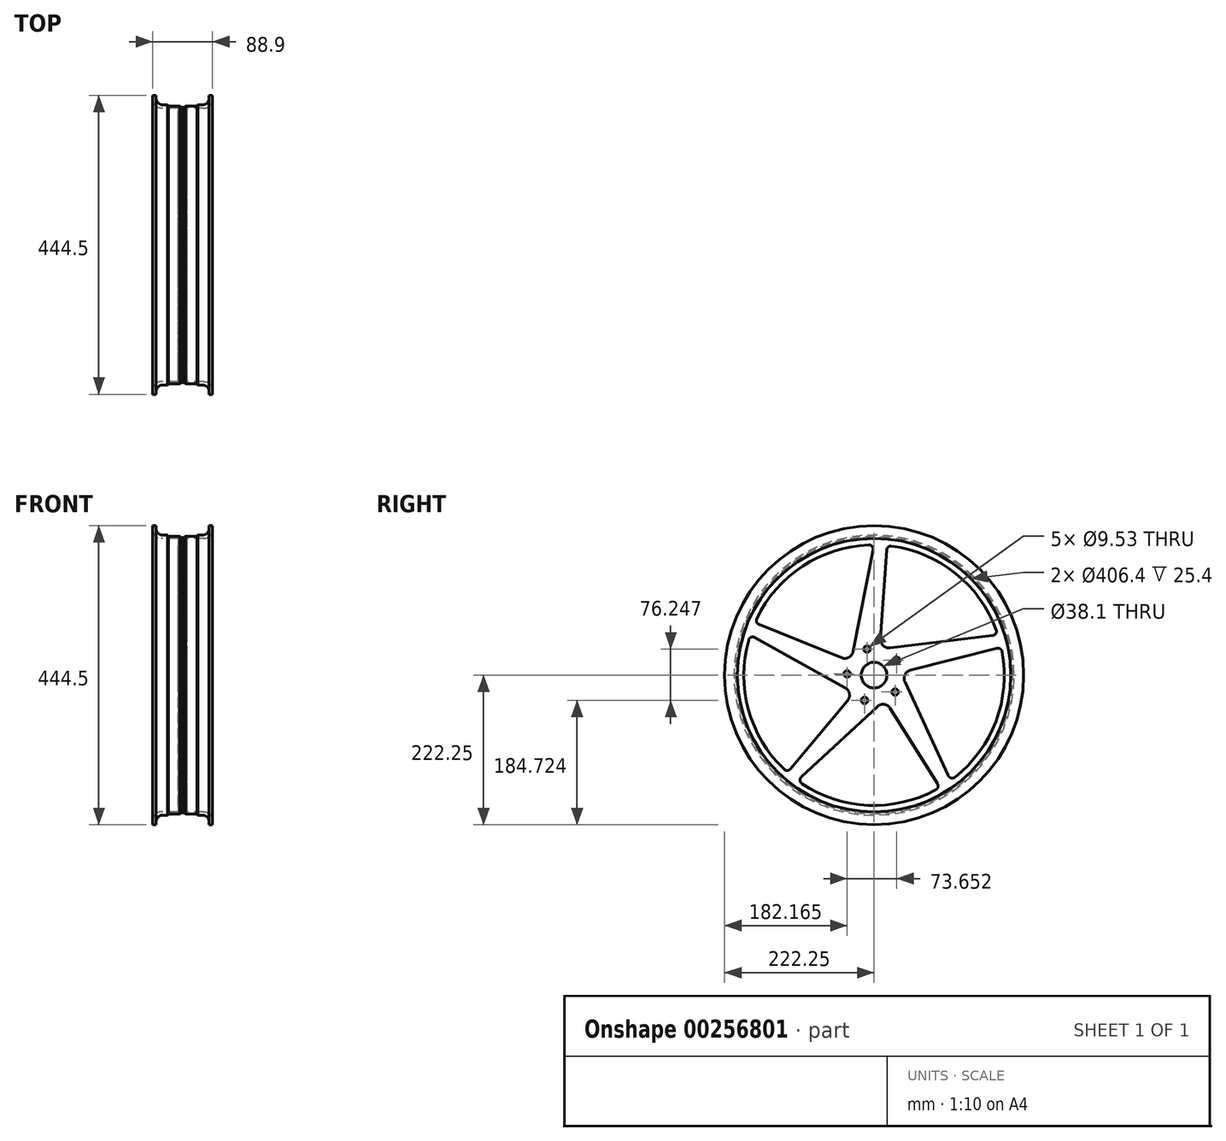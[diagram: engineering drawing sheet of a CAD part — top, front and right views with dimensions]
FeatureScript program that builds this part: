
annotation { "Feature Type Name" : "Feature", "Feature Type Description" : "" }
export const myFeature = defineFeature(function(context is Context, id is Id, definition is map)
    precondition{}
    {
        {
            var Q0;
            Q0=qCreatedBy(makeId("Top.planeOp"),FACE);
            var sketch = newSketch(context, id + "F0", { "sketchPlane" : qUnion([Q0])});
            skLineSegment(sketch, "E0.0", {"start": v(-6.35, 0) * mm, "end": v(-6.35, -203.2) * mm});
            skLineSegment(sketch, "E1.0", {"start": v(6.35, 0) * mm, "end": v(6.35, -203.2) * mm});
            skLineSegment(sketch, "E2", {"start": v(6.35, -203.2) * mm, "end": v(31.75, -203.2) * mm});
            skLineSegment(sketch, "E3", {"start": v(44.45, -215.9) * mm, "end": v(44.45, -222.25) * mm});
            skLineSegment(sketch, "E4", {"start": v(-6.35, -203.2) * mm, "end": v(-31.75, -203.2) * mm});
            skLineSegment(sketch, "E5", {"start": v(44.45, -222.25) * mm, "end": v(39.37, -222.25) * mm});
            skLineSegment(sketch, "E6", {"start": v(-44.45, -215.9) * mm, "end": v(-44.45, -222.25) * mm});
            skLineSegment(sketch, "E7.0", {"start": v(-22.55, -208.28) * mm, "end": v(-29.84, -208.28) * mm});
            skLineSegment(sketch, "E8.0", {"start": v(-39.37, -217.8) * mm, "end": v(-39.37, -222.25) * mm});
            skLineSegment(sketch, "E9.0", {"start": v(39.37, -217.8) * mm, "end": v(39.37, -222.25) * mm});
            skLineSegment(sketch, "E10.trimOffspring", {"start": v(-39.37, -222.25) * mm, "end": v(-44.45, -222.25) * mm});
            skPoint(sketch, "E11.visualSharp", {"position": v(-44.45, -203.2) * mm});
            skArc(sketch, "E11.filletArc", {"start": v(-31.75, -203.2) * mm, "mid": v(-40.73, -206.92) * mm, "end": v(-44.45, -215.9) * mm});
            skPoint(sketch, "E12.visualSharp", {"position": v(-39.37, -208.28) * mm});
            skArc(sketch, "E12.filletArc", {"start": v(-29.84, -208.28) * mm, "mid": v(-36.58, -211.07) * mm, "end": v(-39.37, -217.8) * mm});
            skPoint(sketch, "E13.visualSharp", {"position": v(39.37, -208.28) * mm});
            skArc(sketch, "E13.filletArc", {"start": v(39.37, -217.8) * mm, "mid": v(36.58, -211.07) * mm, "end": v(29.85, -208.28) * mm});
            skPoint(sketch, "E14.visualSharp", {"position": v(44.45, -203.2) * mm});
            skArc(sketch, "E14.filletArc", {"start": v(44.45, -215.9) * mm, "mid": v(40.73, -206.92) * mm, "end": v(31.75, -203.2) * mm});
            skLineSegment(sketch, "E15", {"start": v(29.85, -208.28) * mm, "end": v(22.55, -208.28) * mm});
            skLineSegment(sketch, "E16", {"start": v(-6.35, 0) * mm, "end": v(6.35, 0) * mm});
            skLineSegment(sketch, "E17", {"start": v(-22.55, -208.28) * mm, "end": v(-21.34, -206.26) * mm});
            skLineSegment(sketch, "E18", {"start": v(-21.34, -206.26) * mm, "end": v(-4.07, -206.26) * mm});
            skLineSegment(sketch, "E19", {"start": v(-4.07, -206.26) * mm, "end": v(-2.24, -204.5) * mm});
            skLineSegment(sketch, "E20", {"start": v(-2.24, -204.5) * mm, "end": v(0, -204.5) * mm});
            skLineSegment(sketch, "E21.MirrorCS", {"start": v(22.55, -208.28) * mm, "end": v(21.34, -206.26) * mm});
            skLineSegment(sketch, "E22.MirrorCS", {"start": v(21.34, -206.26) * mm, "end": v(4.07, -206.26) * mm});
            skLineSegment(sketch, "E23.MirrorCS", {"start": v(2.24, -204.5) * mm, "end": v(0, -204.5) * mm});
            skLineSegment(sketch, "E24.MirrorCS", {"start": v(4.07, -206.26) * mm, "end": v(2.24, -204.5) * mm});
            skPoint(sketch, "E25.end.orphan", {"position": v(0, -208.28) * mm});
            skSolve(sketch);
        }
        {
            var Q0;
            Q0=makeQuery(id+"F0.imprint","IMPRINT",FACE,{"disambiguationData":[TD([[makeQuery(id+"F0.imprint","IMPRINT",EDGE,{"derivedFrom":sQuery(id+"F0.wireOp",EDGE,"E0.0")}),1.0]])]});
            var Q1;
            Q1=sQuery(id+"F0.wireOp",EDGE,"E16");
            revolve(context, id + "F1", {"entities" : qUnion([Q0]), "axis" : qUnion([Q1]), "revolveType" : RevolveType.FULL});
        }
        {
            var Q0;
            Q0=makeQuery(id+"F1.opRevolve","SWEPT_FACE",FACE,{"disambiguationData":[OSD([sQuery(id+"F0.wireOp",EDGE,"E0.0")])]});
            var sketch = newSketch(context, id + "F2", { "sketchPlane" : qUnion([Q0])});
            skCircle(sketch, "E26", {"center": v(0, 0) * mm, "radius": 19.05 * mm});
            skArc(sketch, "E27", {"start": v(-25.92, 191.93) * mm, "mid": v(-120.99, 151.23) * mm, "end": v(-181.56, 67.42) * mm});
            skLineSegment(sketch, "E28", {"start": v(-9.61, 54) * mm, "end": v(-18.74, 186.08) * mm});
            skLineSegment(sketch, "E29.1.0", {"start": v(-54.33, 7.55) * mm, "end": v(-182.76, 39.68) * mm});
            skLineSegment(sketch, "E29.2.0", {"start": v(-23.97, -49.34) * mm, "end": v(-94.21, -161.55) * mm});
            skLineSegment(sketch, "E29.3.0", {"start": v(39.52, -38.04) * mm, "end": v(124.53, -139.52) * mm});
            skLineSegment(sketch, "E29.4.0", {"start": v(48.4, 25.83) * mm, "end": v(171.18, 75.32) * mm});
            skLineSegment(sketch, "E30.trimOffspring", {"start": v(-23.8, 40.52) * mm, "end": v(-176.37, 58.9) * mm});
            skPoint(sketch, "E31.orphan", {"position": v(-8.45, 37.15) * mm});
            skLineSegment(sketch, "E32.trimOffspring", {"start": v(-45.9, -10.11) * mm, "end": v(-110.52, -149.53) * mm});
            skPoint(sketch, "E33.orphan", {"position": v(-37.94, 3.45) * mm});
            skLineSegment(sketch, "E34.trimOffspring", {"start": v(31.18, 35.16) * mm, "end": v(1.52, 185.94) * mm});
            skPoint(sketch, "E35.orphan", {"position": v(32.72, 19.51) * mm});
            skLineSegment(sketch, "E36.trimOffspring", {"start": v(43.07, -18.8) * mm, "end": v(177.3, 56.01) * mm});
            skPoint(sketch, "E37.orphan", {"position": v(28.67, -25.1) * mm});
            skPoint(sketch, "E38.orphan", {"position": v(-15, -35.02) * mm});
            skLineSegment(sketch, "E39.trimOffspring", {"start": v(-4.56, -46.77) * mm, "end": v(108.06, -151.32) * mm});
            skPoint(sketch, "E40.visualSharp", {"position": v(-39.43, 3.82) * mm});
            skArc(sketch, "E40.filletArc", {"start": v(-45.9, -10.11) * mm, "mid": v(-45.96, 0.7) * mm, "end": v(-54.33, 7.55) * mm});
            skPoint(sketch, "E41.visualSharp", {"position": v(-8.55, 38.68) * mm});
            skArc(sketch, "E41.filletArc", {"start": v(-23.8, 40.52) * mm, "mid": v(-13.53, 43.92) * mm, "end": v(-9.61, 54) * mm});
            skPoint(sketch, "E42.visualSharp", {"position": v(34.15, 20.09) * mm});
            skArc(sketch, "E42.filletArc", {"start": v(31.18, 35.16) * mm, "mid": v(37.6, 26.44) * mm, "end": v(48.4, 25.83) * mm});
            skPoint(sketch, "E43.visualSharp", {"position": v(29.66, -26.27) * mm});
            skArc(sketch, "E43.filletArc", {"start": v(43.07, -18.8) * mm, "mid": v(36.77, -27.58) * mm, "end": v(39.52, -38.04) * mm});
            skPoint(sketch, "E44.visualSharp", {"position": v(-15.82, -36.32) * mm});
            skArc(sketch, "E44.filletArc", {"start": v(-4.56, -46.77) * mm, "mid": v(-14.87, -43.49) * mm, "end": v(-23.97, -49.34) * mm});
            skArc(sketch, "E45.trimOffspring", {"start": v(174.53, 83.97) * mm, "mid": v(106.44, 161.8) * mm, "end": v(8.02, 193.5) * mm});
            skArc(sketch, "E46.trimOffspring", {"start": v(-190.55, 34.65) * mm, "mid": v(-181.22, -68.33) * mm, "end": v(-120.23, -151.84) * mm});
            skArc(sketch, "E47.trimOffspring", {"start": v(-91.84, -170.51) * mm, "mid": v(8.99, -193.47) * mm, "end": v(107.26, -161.26) * mm});
            skArc(sketch, "E48.trimOffspring", {"start": v(133.79, -140.04) * mm, "mid": v(186.78, -51.23) * mm, "end": v(186.51, 52.17) * mm});
            skPoint(sketch, "E49.visualSharp", {"position": v(-184.2, 59.85) * mm});
            skArc(sketch, "E49.filletArc", {"start": v(-181.56, 67.42) * mm, "mid": v(-181.03, 61.9) * mm, "end": v(-176.37, 58.9) * mm});
            skPoint(sketch, "E50.visualSharp", {"position": v(-189.22, 41.3) * mm});
            skArc(sketch, "E50.filletArc", {"start": v(-182.76, 39.68) * mm, "mid": v(-187.74, 38.85) * mm, "end": v(-190.55, 34.65) * mm});
            skPoint(sketch, "E51.visualSharp", {"position": v(-19.2, 192.72) * mm});
            skArc(sketch, "E51.filletArc", {"start": v(-18.74, 186.08) * mm, "mid": v(-21.06, 190.56) * mm, "end": v(-25.92, 191.93) * mm});
            skPoint(sketch, "E52.visualSharp", {"position": v(0, 193.68) * mm});
            skArc(sketch, "E52.filletArc", {"start": v(8.02, 193.5) * mm, "mid": v(2.93, 191.3) * mm, "end": v(1.52, 185.94) * mm});
            skPoint(sketch, "E53.visualSharp", {"position": v(177.36, 77.81) * mm});
            skArc(sketch, "E53.filletArc", {"start": v(171.18, 75.32) * mm, "mid": v(174.73, 78.92) * mm, "end": v(174.53, 83.97) * mm});
            skPoint(sketch, "E54.visualSharp", {"position": v(184.2, 59.85) * mm});
            skArc(sketch, "E54.filletArc", {"start": v(186.51, 52.17) * mm, "mid": v(182.84, 56.33) * mm, "end": v(177.3, 56.01) * mm});
            skPoint(sketch, "E55.visualSharp", {"position": v(128.81, -144.63) * mm});
            skArc(sketch, "E55.filletArc", {"start": v(124.53, -139.52) * mm, "mid": v(129.05, -141.79) * mm, "end": v(133.79, -140.04) * mm});
            skPoint(sketch, "E56.visualSharp", {"position": v(113.84, -156.69) * mm});
            skArc(sketch, "E56.filletArc", {"start": v(107.26, -161.26) * mm, "mid": v(110.07, -156.49) * mm, "end": v(108.06, -151.32) * mm});
            skPoint(sketch, "E57.visualSharp", {"position": v(-97.75, -167.2) * mm});
            skArc(sketch, "E57.filletArc", {"start": v(-94.21, -161.55) * mm, "mid": v(-94.97, -166.55) * mm, "end": v(-91.84, -170.51) * mm});
            skPoint(sketch, "E58.visualSharp", {"position": v(-113.84, -156.69) * mm});
            skArc(sketch, "E58.filletArc", {"start": v(-120.23, -151.84) * mm, "mid": v(-114.82, -153.04) * mm, "end": v(-110.52, -149.53) * mm});
            skSolve(sketch);
        }
        {
            var Q0;
            Q0=makeQuery(id+"F2.imprint","IMPRINT",FACE,{"disambiguationData":[TD([[makeQuery(id+"F2.imprint","IMPRINT",EDGE,{"derivedFrom":sQuery(id+"F2.wireOp",EDGE,"E26")}),1.0]])]});
            var Q1;
            Q1=makeQuery(id+"F2.imprint","IMPRINT",FACE,{"disambiguationData":[TD([[makeQuery(id+"F2.imprint","IMPRINT",EDGE,{"derivedFrom":sQuery(id+"F2.wireOp",EDGE,"E27")}),1.0]])]});
            var Q2;
            Q2=makeQuery(id+"F2.imprint","IMPRINT",FACE,{"disambiguationData":[TD([[makeQuery(id+"F2.imprint","IMPRINT",EDGE,{"derivedFrom":sQuery(id+"F2.wireOp",EDGE,"E29.1.0")}),1.0]])]});
            var Q3;
            Q3=makeQuery(id+"F2.imprint","IMPRINT",FACE,{"disambiguationData":[TD([[makeQuery(id+"F2.imprint","IMPRINT",EDGE,{"derivedFrom":sQuery(id+"F2.wireOp",EDGE,"E29.2.0")}),1.0]])]});
            var Q4;
            Q4=makeQuery(id+"F2.imprint","IMPRINT",FACE,{"disambiguationData":[TD([[makeQuery(id+"F2.imprint","IMPRINT",EDGE,{"derivedFrom":sQuery(id+"F2.wireOp",EDGE,"E29.3.0")}),1.0]])]});
            var Q5;
            Q5=makeQuery(id+"F2.imprint","IMPRINT",FACE,{"disambiguationData":[TD([[makeQuery(id+"F2.imprint","IMPRINT",EDGE,{"derivedFrom":sQuery(id+"F2.wireOp",EDGE,"E29.4.0")}),1.0]])]});
            extrude(context, id + "F3", {"entities" : qUnion([Q0, Q1, Q2, Q3, Q4, Q5]), "operationType" : NewBodyOperationType.REMOVE, "endBound" : BoundingType.THROUGH_ALL, "oppositeDirection" : true, "depth" : 25.4 * mm});
        }
        {
            var Q0;
            Q0=makeQuery(id+"F3.boolean.opBoolean","COPY",EDGE,{"derivedFrom":makeQuery(id+"F3.opExtrude","CAP_EDGE",EDGE,{"disambiguationData":[OSD([sQuery(id+"F2.wireOp",EDGE,"E30.trimOffspring")])],"isStart":true})});
            var Q1;
            Q1=makeQuery(id+"F3.boolean.opBoolean","COPY",EDGE,{"derivedFrom":makeQuery(id+"F3.opExtrude","CAP_EDGE",EDGE,{"disambiguationData":[OSD([sQuery(id+"F2.wireOp",EDGE,"E34.trimOffspring")])],"isStart":true})});
            var Q2;
            Q2=makeQuery(id+"F3.boolean.opBoolean","COPY",EDGE,{"derivedFrom":makeQuery(id+"F3.opExtrude","CAP_EDGE",EDGE,{"disambiguationData":[OSD([sQuery(id+"F2.wireOp",EDGE,"E36.trimOffspring")])],"isStart":true})});
            var Q3;
            Q3=makeQuery(id+"F3.boolean.opBoolean","COPY",EDGE,{"derivedFrom":makeQuery(id+"F3.opExtrude","CAP_EDGE",EDGE,{"disambiguationData":[OSD([sQuery(id+"F2.wireOp",EDGE,"E29.2.0")])],"isStart":true})});
            var Q4;
            Q4=makeQuery(id+"F3.boolean.opBoolean","COPY",EDGE,{"derivedFrom":makeQuery(id+"F3.opExtrude","CAP_EDGE",EDGE,{"disambiguationData":[OSD([sQuery(id+"F2.wireOp",EDGE,"E32.trimOffspring")])],"isStart":true})});
            var Q5;
            Q5=makeQuery(id+"F3.boolean.opBoolean","INTERSECT",EDGE,{"derivedFrom":[makeQuery(id+"F1.opRevolve","SWEPT_FACE",FACE,{"disambiguationData":[OSD([sQuery(id+"F0.wireOp",EDGE,"E1.0")])]}),makeQuery(id+"F3.opExtrude","SWEPT_FACE",FACE,{"disambiguationData":[OSD([sQuery(id+"F2.wireOp",EDGE,"E39.trimOffspring")])]})]});
            var Q6;
            Q6=makeQuery(id+"F3.boolean.opBoolean","INTERSECT",EDGE,{"derivedFrom":[makeQuery(id+"F1.opRevolve","SWEPT_FACE",FACE,{"disambiguationData":[OSD([sQuery(id+"F0.wireOp",EDGE,"E1.0")])]}),makeQuery(id+"F3.opExtrude","SWEPT_FACE",FACE,{"disambiguationData":[OSD([sQuery(id+"F2.wireOp",EDGE,"E32.trimOffspring")])]})]});
            var Q7;
            Q7=makeQuery(id+"F3.boolean.opBoolean","INTERSECT",EDGE,{"derivedFrom":[makeQuery(id+"F1.opRevolve","SWEPT_FACE",FACE,{"disambiguationData":[OSD([sQuery(id+"F0.wireOp",EDGE,"E1.0")])]}),makeQuery(id+"F3.opExtrude","SWEPT_FACE",FACE,{"disambiguationData":[OSD([sQuery(id+"F2.wireOp",EDGE,"E28")])]})]});
            var Q8;
            Q8=makeQuery(id+"F3.boolean.opBoolean","INTERSECT",EDGE,{"derivedFrom":[makeQuery(id+"F1.opRevolve","SWEPT_FACE",FACE,{"disambiguationData":[OSD([sQuery(id+"F0.wireOp",EDGE,"E1.0")])]}),makeQuery(id+"F3.opExtrude","SWEPT_FACE",FACE,{"disambiguationData":[OSD([sQuery(id+"F2.wireOp",EDGE,"E29.4.0")])]})]});
            var Q9;
            Q9=makeQuery(id+"F3.boolean.opBoolean","INTERSECT",EDGE,{"derivedFrom":[makeQuery(id+"F1.opRevolve","SWEPT_FACE",FACE,{"disambiguationData":[OSD([sQuery(id+"F0.wireOp",EDGE,"E1.0")])]}),makeQuery(id+"F3.opExtrude","SWEPT_FACE",FACE,{"disambiguationData":[OSD([sQuery(id+"F2.wireOp",EDGE,"E29.3.0")])]})]});
            fillet(context, id + "F4", {"entities" : qUnion([Q0, Q1, Q2, Q3, Q4, Q5, Q6, Q7, Q8, Q9]), "radius" : 2.54 * mm, "tangentPropagation" : true, "allowEdgeOverflow" : false});
        }
        {
            var Q0;
            Q0=makeQuery(id+"F2.imprint","IMPRINT",FACE,{"disambiguationData":[TD([[makeQuery(id+"F2.imprint","IMPRINT",EDGE,{"derivedFrom":sQuery(id+"F2.wireOp",EDGE,"E26")}),-1.0]])]});
            var sketch = newSketch(context, id + "F5", { "sketchPlane" : qUnion([Q0])});
            skCircle(sketch, "E59", {"center": v(10.55, 38.72) * mm, "radius": 4.76 * mm});
            skCircle(sketch, "E60.1.0", {"center": v(-33.57, 22) * mm, "radius": 4.76 * mm});
            skCircle(sketch, "E60.2.0", {"center": v(-31.3, -25.13) * mm, "radius": 4.76 * mm});
            skCircle(sketch, "E60.3.0", {"center": v(14.23, -37.53) * mm, "radius": 4.76 * mm});
            skCircle(sketch, "E60.4.0", {"center": v(40.09, 1.93) * mm, "radius": 4.76 * mm});
            skPoint(sketch, "E60.center", {"position": v(0, 0) * mm});
            skSolve(sketch);
        }
        {
            var Q0;
            Q0 = qSketchRegion(id + "F5", true);
            extrude(context, id + "F6", {"entities" : qUnion([Q0]), "operationType" : NewBodyOperationType.REMOVE, "endBound" : BoundingType.THROUGH_ALL, "oppositeDirection" : true, "depth" : 25.4 * mm});
        }
    });
